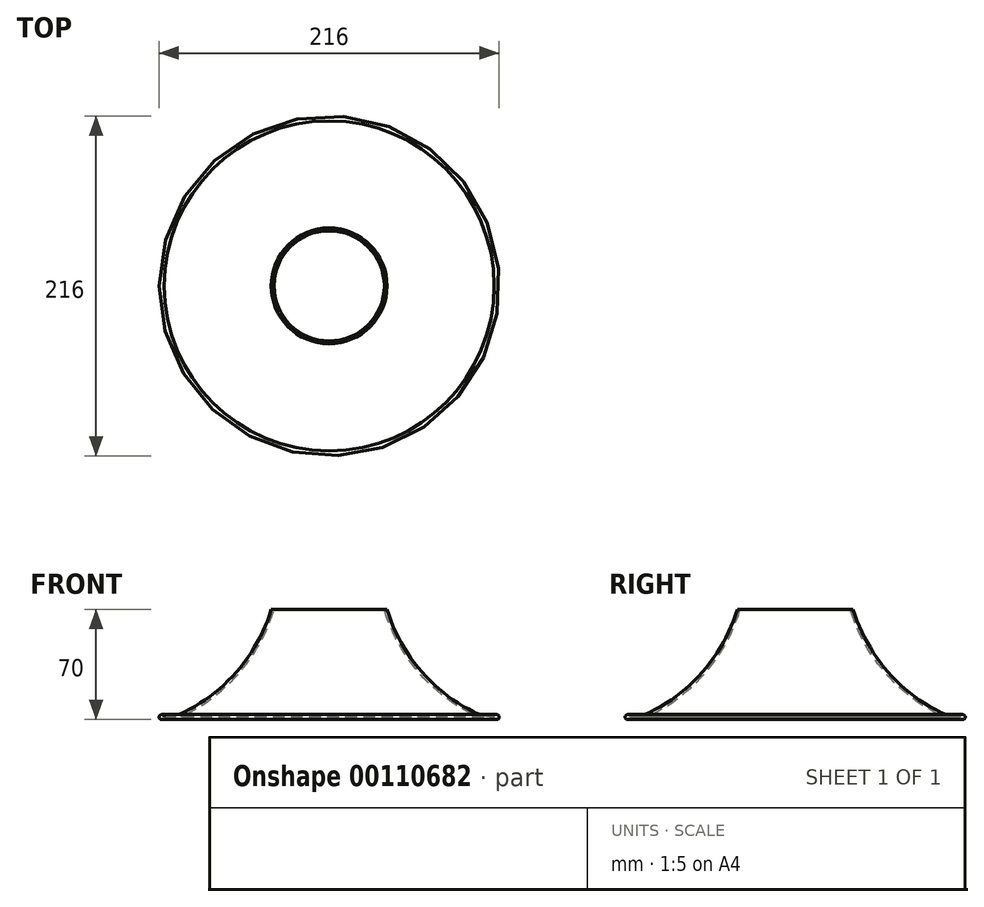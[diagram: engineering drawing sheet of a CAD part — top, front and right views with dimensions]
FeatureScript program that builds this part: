
annotation { "Feature Type Name" : "Feature", "Feature Type Description" : "" }
export const myFeature = defineFeature(function(context is Context, id is Id, definition is map)
    precondition{}
    {
        {
            var Q0;
            Q0=qCreatedBy(makeId("Front.planeOp"),FACE);
            var sketch = newSketch(context, id + "F0", { "sketchPlane" : qUnion([Q0])});
            skLineSegment(sketch, "E0", {"start": v(0, 0) * mm, "end": v(106.4, 0) * mm, "construction": true});
            skLineSegment(sketch, "E1", {"start": v(0, 0) * mm, "end": v(0, 70) * mm, "construction": true});
            skArc(sketch, "E2", {"start": v(106.4, 0) * mm, "mid": v(107.57, 2.7) * mm, "end": v(104.8, 1.7) * mm});
            skArc(sketch, "E3", {"start": v(35, 70) * mm, "mid": v(56.15, 30.92) * mm, "end": v(91.05, 3.4) * mm});
            skLineSegment(sketch, "E4", {"start": v(35, 70) * mm, "end": v(36.78, 70) * mm});
            skLineSegment(sketch, "E5", {"start": v(106.4, 0) * mm, "end": v(105.4, 0) * mm});
            skArc(sketch, "E6", {"start": v(91.05, 3.4) * mm, "mid": v(98.03, 0.86) * mm, "end": v(105.4, 0) * mm});
            skLineSegment(sketch, "E7", {"start": v(105.4, 32.04) * mm, "end": v(91.05, 3.4) * mm, "construction": true});
            skLineSegment(sketch, "E8", {"start": v(35, 70) * mm, "end": v(140.32, 101.74) * mm, "construction": true});
            skArc(sketch, "E9.1", {"start": v(91.8, 4.91) * mm, "mid": v(98.13, 2.58) * mm, "end": v(104.8, 1.7) * mm});
            skArc(sketch, "E9.2", {"start": v(36.78, 70) * mm, "mid": v(57.62, 31.82) * mm, "end": v(91.8, 4.91) * mm});
            skLineSegment(sketch, "E10", {"start": v(0, 70) * mm, "end": v(35, 70) * mm, "construction": true});
            skLineSegment(sketch, "E11", {"start": v(108, 1.6) * mm, "end": v(108, -17.05) * mm, "construction": true});
            skSolve(sketch);
        }
        {
            var Q0;
            Q0=qSketchRegion(id+"F0",true);
            var Q1;
            Q1=sQuery(id+"F0.wireOp",EDGE,"E1");
            revolve(context, id + "F1", {"entities" : qUnion([Q0]), "axis" : qUnion([Q1]), "revolveType" : RevolveType.FULL});
        }
    });
